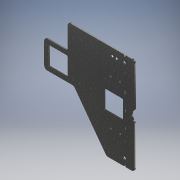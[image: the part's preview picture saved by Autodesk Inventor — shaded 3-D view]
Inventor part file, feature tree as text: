
AUTODESK INVENTOR PART (.ipt)
format: ipt  version: 2017 (Build 210142000, 142)  size: 276,480 bytes
history: native  units: mm
features: fillet x4, extrude x3, sketch x3, other x1
ambient origin geometry x8: Origin, YZ Plane, XZ Plane, XY Plane, X Axis, Y Axis, Z Axis, Center Point
bodies: Body1 (feature_tree)
feature tree (11):
  other  "Sólido1"
  extrude  "Extrusión1"  Depth=101.6mm
  fillet  "Empalme1"  Radius=95.25mm
  fillet  "Empalme2"  Radius=111.125mm
  extrude  "Extrusión2"  Depth=5.0mm TaperAngle=0.0deg
  fillet  "Empalme3"  Radius=12.7mm
  extrude  "Extrusión3"  Depth=76.2mm
  fillet  "Empalme4"  Radius=17.4625mm
  sketch  "Boceto1"  dims[d0=273.05mm d1=101.6mm d2=95.25mm d3=111.125mm]
  sketch  "Boceto2"  dims[d4=393.7mm d7=5.0mm d8=0.0mm d9=12.7mm]
  sketch  "Boceto3"  dims[d10=6.35mm d11=76.2mm d17=17.4625mm d18=19.05mm d19=76.2mm d20=5.55625mm d22=6.35mm d24=38.1mm d27=8.73125mm d38=76.2mm d39=76.2mm d40=158.75mm d42=12.7mm d43=28.575mm d44=42.664062mm d45=8.929688mm d46=0.0mm d47=12.7mm d50=114.3mm d51=133.35mm d52=38.1mm d53=5.55625mm d54=6.35mm d55=47.625mm d56=8.73125mm d57=98.028125mm d58=38.1mm d59=53.975mm d60=53.975mm d61=184.15mm d62=184.15mm d63=38.1mm d64=8.73125mm d65=8.73125mm d66=98.028125mm d67=42.664062mm d68=28.575mm d69=5.55625mm d70=5.55625mm d71=5.55625mm d72=13.096875mm d73=13.096875mm d74=13.096875mm d75=38.1mm d80=63.5mm d81=63.5mm d82=127.0mm d83=3.571875mm d86=12.7mm d87=22.225mm d88=22.225mm d89=25.4mm d90=0.0mm d91=4.7625mm d92=7.9375mm d93=7.9375mm d94=25.4mm d96=25.4mm d97=25.4mm d98=25.4mm]
